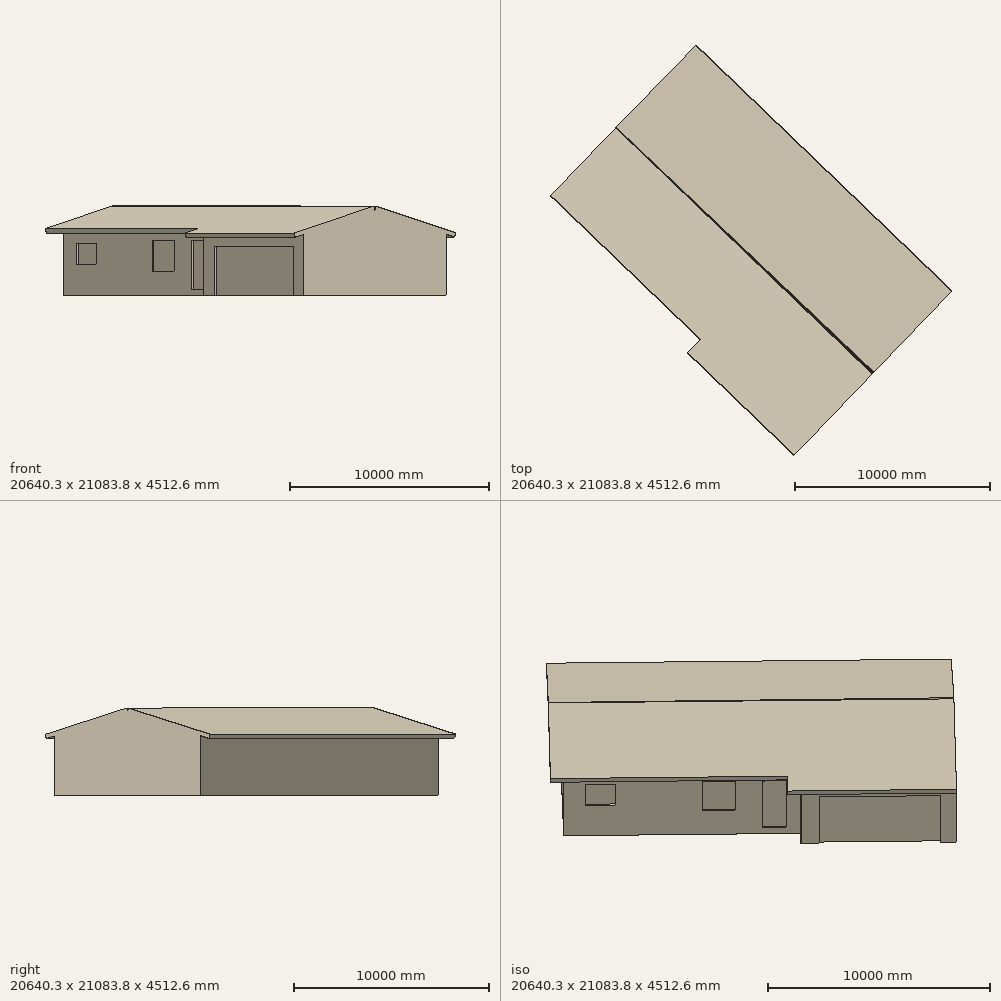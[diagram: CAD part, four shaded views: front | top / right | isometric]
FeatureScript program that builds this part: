
annotation { "Feature Type Name" : "Feature", "Feature Type Description" : "" }
export const myFeature = defineFeature(function(context is Context, id is Id, definition is map)
    precondition{}
    {
        {
            var Q0;
            Q0=qCreatedBy(makeId("Top.planeOp"),FACE);
            var sketch = newSketch(context, id + "F0", { "sketchPlane" : qUnion([Q0])});
            skLineSegment(sketch, "E0", {"start": v(9394.03, -16083.05) * mm, "end": v(22143.99, -28323.02) * mm});
            skLineSegment(sketch, "E1", {"start": v(22143.99, -28323.02) * mm, "end": v(14927.08, -35840.63) * mm});
            skLineSegment(sketch, "E2", {"start": v(14927.08, -35840.63) * mm, "end": v(9880.3, -30995.71) * mm});
            skLineSegment(sketch, "E3", {"start": v(9394.03, -16083.05) * mm, "end": v(2837.52, -22912.75) * mm});
            skLineSegment(sketch, "E4", {"start": v(2837.52, -22912.75) * mm, "end": v(10540.7, -30307.8) * mm});
            skLineSegment(sketch, "E5", {"start": v(10540.7, -30307.8) * mm, "end": v(9880.3, -30995.71) * mm});
            skSolve(sketch);
        }
        {
            var Q0;
            Q0 = qSketchRegion(id + "F0", true);
            extrude(context, id + "F1", {"entities" : qUnion([Q0]), "depth" : 4267.2 * mm, "offsetDistance" : 30.48 * mm});
        }
        {
            var Q0;
            Q0=makeQuery(id+"F1.opExtrude","SWEPT_FACE",FACE,{"disambiguationData":[OSD([sQuery(id+"F0.wireOp",EDGE,"E1")])]});
            var sketch = newSketch(context, id + "F2", { "sketchPlane" : qUnion([Q0])});
            skLineSegment(sketch, "E6", {"start": v(-15517.5, 4267.2) * mm, "end": v(-5096.44, 4267.2) * mm});
            skLineSegment(sketch, "E7", {"start": v(-5096.44, 4267.2) * mm, "end": v(-5025.37, 3048) * mm});
            skLineSegment(sketch, "E8", {"start": v(-5025.37, 3048) * mm, "end": v(-10306.97, 4267.2) * mm});
            skLineSegment(sketch, "E9", {"start": v(-10306.97, 4267.2) * mm, "end": v(-15517.5, 3048) * mm});
            skLineSegment(sketch, "E10", {"start": v(-15517.5, 3048) * mm, "end": v(-15517.5, 4267.2) * mm});
            skPoint(sketch, "E11", {"position": v(-15517.5, 0) * mm});
            skPoint(sketch, "E12", {"position": v(-10306.97, 0) * mm});
            skSolve(sketch);
        }
        {
            var Q0;
            Q0 = qSketchRegion(id + "F2", true);
            extrude(context, id + "F3", {"entities" : qUnion([Q0]), "operationType" : NewBodyOperationType.REMOVE, "endBound" : BoundingType.THROUGH_ALL, "oppositeDirection" : true, "depth" : 10972.8 * mm, "offsetDistance" : 30.48 * mm});
        }
        {
            var Q0;
            Q0=makeQuery(id+"F1.opExtrude","SWEPT_FACE",FACE,{"disambiguationData":[OSD([sQuery(id+"F0.wireOp",EDGE,"E2")])]});
            var sketch = newSketch(context, id + "F4", { "sketchPlane" : qUnion([Q0])});
            skLineSegment(sketch, "E13.bottom", {"start": v(29416.78, 0) * mm, "end": v(34903.18, 0) * mm});
            skLineSegment(sketch, "E13.top", {"start": v(29416.78, 2438.4) * mm, "end": v(34903.18, 2438.4) * mm});
            skLineSegment(sketch, "E13.left", {"start": v(29416.78, 0) * mm, "end": v(29416.78, 2438.4) * mm});
            skLineSegment(sketch, "E13.right", {"start": v(34903.18, 0) * mm, "end": v(34903.18, 2438.4) * mm});
            skSolve(sketch);
        }
        {
            var Q0;
            Q0 = qSketchRegion(id + "F4", true);
            extrude(context, id + "F5", {"entities" : qUnion([Q0]), "operationType" : NewBodyOperationType.REMOVE, "oppositeDirection" : true, "depth" : 152.4 * mm, "offsetDistance" : 30.48 * mm});
        }
        {
            var Q0;
            Q0=makeQuery(id+"F1.opExtrude","SWEPT_FACE",FACE,{"disambiguationData":[OSD([sQuery(id+"F0.wireOp",EDGE,"E4")])]});
            var sketch = newSketch(context, id + "F6", { "sketchPlane" : qUnion([Q0])});
            skLineSegment(sketch, "E14.bottom", {"start": v(26893.19, 304.8) * mm, "end": v(27959.99, 304.8) * mm});
            skLineSegment(sketch, "E14.top", {"start": v(26893.19, 2743.2) * mm, "end": v(27959.99, 2743.2) * mm});
            skLineSegment(sketch, "E14.left", {"start": v(26893.19, 304.8) * mm, "end": v(26893.19, 2743.2) * mm});
            skLineSegment(sketch, "E14.right", {"start": v(27959.99, 304.8) * mm, "end": v(27959.99, 2743.2) * mm});
            skLineSegment(sketch, "E15.bottom", {"start": v(25679.77, 1222.51) * mm, "end": v(24155.77, 1222.51) * mm});
            skLineSegment(sketch, "E15.top", {"start": v(25679.77, 2746.51) * mm, "end": v(24155.77, 2746.51) * mm});
            skLineSegment(sketch, "E15.left", {"start": v(25679.77, 1222.51) * mm, "end": v(25679.77, 2746.51) * mm});
            skLineSegment(sketch, "E15.right", {"start": v(24155.77, 1222.51) * mm, "end": v(24155.77, 2746.51) * mm});
            skLineSegment(sketch, "E16.bottom", {"start": v(20242.03, 1570.04) * mm, "end": v(18881.57, 1570.04) * mm});
            skLineSegment(sketch, "E16.top", {"start": v(20242.03, 2633.05) * mm, "end": v(18881.57, 2633.05) * mm});
            skLineSegment(sketch, "E16.left", {"start": v(20242.03, 1570.04) * mm, "end": v(20242.03, 2633.05) * mm});
            skLineSegment(sketch, "E16.right", {"start": v(18881.57, 1570.04) * mm, "end": v(18881.57, 2633.05) * mm});
            skSolve(sketch);
        }
        {
            var Q0;
            Q0 = qSketchRegion(id + "F6", true);
            extrude(context, id + "F7", {"entities" : qUnion([Q0]), "operationType" : NewBodyOperationType.REMOVE, "oppositeDirection" : true, "depth" : 100.58 * mm, "offsetDistance" : 30.48 * mm});
        }
        {
            var Q0;
            Q0=makeQuery(id+"F3.boolean.opBoolean","COPY",FACE,{"derivedFrom":makeQuery(id+"F3.opExtrude","SWEPT_FACE",FACE,{"disambiguationData":[OSD([sQuery(id+"F2.wireOp",EDGE,"E9")])]})});
            var sketch = newSketch(context, id + "F8", { "sketchPlane" : qUnion([Q0])});
            skLineSegment(sketch, "E17.0", {"start": v(10183.13, -30085.1) * mm, "end": v(15739.27, -35278.72) * mm});
            skLineSegment(sketch, "E17.1", {"start": v(10851.9, -29369.65) * mm, "end": v(10183.13, -30085.1) * mm});
            skLineSegment(sketch, "E17.2", {"start": v(3051.01, -22077.75) * mm, "end": v(10851.9, -29369.65) * mm});
            skLineSegment(sketch, "E18", {"start": v(15739.27, -35278.72) * mm, "end": v(19809.77, -30924.09) * mm});
            skLineSegment(sketch, "E19", {"start": v(19809.77, -30924.09) * mm, "end": v(6452.74, -18438.57) * mm});
            skLineSegment(sketch, "E20", {"start": v(6452.74, -18438.57) * mm, "end": v(3051.01, -22077.75) * mm});
            skSolve(sketch);
        }
        {
            var Q0;
            Q0 = qSketchRegion(id + "F8", true);
            extrude(context, id + "F9", {"entities" : qUnion([Q0]), "operationType" : NewBodyOperationType.ADD, "depth" : 228.6 * mm, "offsetDistance" : 30.48 * mm});
        }
        {
            var Q0;
            Q0=makeQuery(id+"F3.boolean.opBoolean","COPY",FACE,{"derivedFrom":makeQuery(id+"F3.opExtrude","SWEPT_FACE",FACE,{"disambiguationData":[OSD([sQuery(id+"F2.wireOp",EDGE,"E8")])]})});
            var sketch = newSketch(context, id + "F10", { "sketchPlane" : qUnion([Q0])});
            skLineSegment(sketch, "E21", {"start": v(18474.5, -32346.99) * mm, "end": v(5052.92, -19930.47) * mm});
            skLineSegment(sketch, "E22", {"start": v(5052.92, -19930.47) * mm, "end": v(9220.02, -15533.23) * mm});
            skLineSegment(sketch, "E23", {"start": v(9220.02, -15533.23) * mm, "end": v(22543.97, -27996.47) * mm});
            skLineSegment(sketch, "E24", {"start": v(22543.97, -27996.47) * mm, "end": v(18474.5, -32346.99) * mm});
            skSolve(sketch);
        }
        {
            var Q0;
            Q0 = qSketchRegion(id + "F10", true);
            extrude(context, id + "F11", {"entities" : qUnion([Q0]), "operationType" : NewBodyOperationType.ADD, "depth" : 228.6 * mm, "offsetDistance" : 30.48 * mm});
        }
    });
